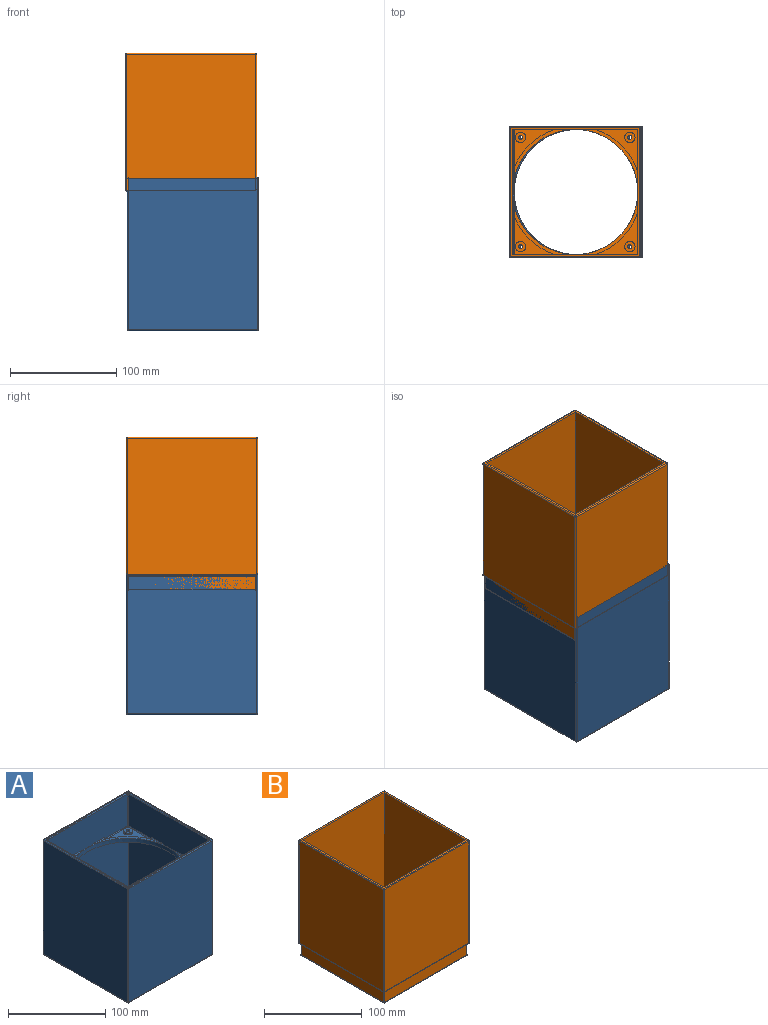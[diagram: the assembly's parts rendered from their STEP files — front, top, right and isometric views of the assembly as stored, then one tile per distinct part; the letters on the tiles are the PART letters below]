
ASSEMBLY  parts=2 mates=1
PART A: 108 faces, bbox 124.4x124.4x145.4 mm
  f0: plane 47.18x47.18mm, normal (0,0,1), area 183.2mm2, adj f14,f21,f98,f100,f105,f107
  f1: plane 47.18x47.18mm, normal (0,0,1), area 183.2mm2, adj f14,f29,f70,f71,f76,f77
  f2: plane 47.18x47.18mm, normal (0,0,1), area 183.2mm2, adj f14,f25,f62,f63,f66,f67
  f3: plane 9.8x9.8mm, normal (0,0,1), area 64.1mm2, adj f13,f31
  f4: plane 9.8x9.8mm, normal (0,0,1), area 64.1mm2, adj f11,f28
  f5: plane 47.18x47.18mm, normal (0,0,1), area 183.2mm2, adj f14,f33,f74,f75,f79,f80
  f6: plane 9.8x9.8mm, normal (0,0,1), area 64.1mm2, adj f12,f22
  f7: plane 9.8x9.8mm, normal (0,0,1), area 64.1mm2, adj f15,f19
  f8: plane 143x122mm, normal (1,0,0), area 17446mm2, adj f43,f44,f53,f54
  f9: plane 143x122mm, normal (0,1,0), area 17446mm2, adj f40,f44,f45,f46
  f10: plane 143x122mm, normal (-1,0,0), area 17446mm2, adj f46,f47,f55,f56
  f11: cylinder r=1.9mm len=5mm, axis (0,0,-1), area 59.7mm2, adj f4,f17
  f12: cylinder r=1.9mm len=5mm, axis (0,0,-1), area 59.7mm2, adj f6,f17
  f13: cylinder r=1.9mm len=5mm, axis (0,0,-1), area 59.7mm2, adj f3,f17
  f14: cylinder r=59mm len=118mm, axis (0,0,-1), area 1853.5mm2, adj f0,f1,f2,f5,f17,f60,f61,f64
  f15: cylinder r=1.9mm len=5mm, axis (0,0,-1), area 59.7mm2, adj f7,f17
  f16: plane 143x122mm, normal (0,-1,0), area 17446mm2, adj f48,f53,f56,f59
  f17: plane 121x121mm, normal (0,0,-1), area 3659.8mm2, adj f11,f12,f13,f14,f15,f35,f36,f37
  f18: plane 34.4x34.4mm, normal (0,0,1), area 385.9mm2, adj f19,f21,f100,f102,f104,f105
  f19: cylinder r=4.9mm len=9.8mm, axis (0,0,-1), area 61.6mm2, adj f7,f18
  f20: plane 116.35x40.35mm, normal (0,-1,0), area 4550mm2, adj f69,f75,f80,f85,f92,f95,f97,f98
  f21: cylinder r=62mm len=32.87mm, axis (0,0,-1), area 95.3mm2, adj f0,f18,f100,f105
  f22: cylinder r=4.9mm len=9.8mm, axis (0,0,-1), area 61.6mm2, adj f6,f24
  f23: plane 116.35x40.35mm, normal (-1,0,0), area 4550mm2, adj f61,f63,f67,f68,f73,f74,f79,f83
  f24: plane 34.4x34.4mm, normal (0,0,1), area 385.9mm2, adj f22,f25,f66,f67,f72,f73
  f25: cylinder r=62mm len=32.87mm, axis (0,0,-1), area 95.3mm2, adj f2,f24,f66,f67
  f26: plane 34.4x34.4mm, normal (0,0,1), area 385.9mm2, adj f28,f29,f76,f77,f81,f82
  f27: plane 116.35x40.35mm, normal (1,0,0), area 4550mm2, adj f64,f70,f76,f81,f89,f96,f101,f104
  f28: cylinder r=4.9mm len=9.8mm, axis (0,0,-1), area 61.6mm2, adj f4,f26
  f29: cylinder r=62mm len=32.87mm, axis (0,0,-1), area 95.3mm2, adj f1,f26,f76,f77
  f30: plane 116.35x40.35mm, normal (0,1,0), area 4550mm2, adj f60,f62,f65,f66,f71,f72,f77,f82
  f31: cylinder r=4.9mm len=9.8mm, axis (0,0,-1), area 61.6mm2, adj f3,f32
  f32: plane 34.4x34.4mm, normal (0,0,1), area 385.9mm2, adj f31,f33,f79,f80,f84,f85
  f33: cylinder r=62mm len=32.87mm, axis (0,0,-1), area 95.3mm2, adj f5,f32,f79,f80
  f34: plane 122x122mm, normal (0,0,1), area 487.4mm2, adj f40,f43,f47,f48,f87,f90,f91,f93
  f35: plane 121x100mm, normal (1,0,0), area 12100mm2, adj f17,f36,f38,f39
  f36: plane 121x100mm, normal (0,1,0), area 12100mm2, adj f17,f35,f37,f39
  f37: plane 121x100mm, normal (-1,0,0), area 12100mm2, adj f17,f36,f38,f39
  f38: plane 121x100mm, normal (0,-1,0), area 12100mm2, adj f17,f35,f37,f39
  f39: plane 122x122mm, normal (0,0,-1), area 243mm2, adj f35,f36,f37,f38,f45,f54,f55,f59
  f40: cylinder r=1mm len=122mm, axis (1,0,0), area 191.6mm2, adj f9,f34,f41,f42
  f41: sphere r=1mm, area 1.6mm2, adj f40,f43,f44
  f42: sphere r=1mm, area 1.6mm2, adj f40,f46,f47
  f43: cylinder r=1mm len=122mm, axis (0,-1,0), area 191.6mm2, adj f8,f34,f41,f49
  f44: cylinder r=1mm len=143mm, axis (0,0,1), area 224.6mm2, adj f8,f9,f41,f50
  f45: cylinder r=1mm len=122mm, axis (1,0,0), area 191.6mm2, adj f9,f39,f50,f51
  f46: cylinder r=1mm len=143mm, axis (0,0,-1), area 224.6mm2, adj f9,f10,f42,f51
  f47: cylinder r=1mm len=122mm, axis (0,1,0), area 191.6mm2, adj f10,f34,f42,f52
  f48: cylinder r=1mm len=122mm, axis (-1,0,0), area 191.6mm2, adj f16,f34,f49,f52
  f49: sphere r=1mm, area 1.6mm2, adj f43,f48,f53
  f50: sphere r=1mm, area 1.6mm2, adj f44,f45,f54
  f51: sphere r=1mm, area 1.6mm2, adj f45,f46,f55
  f52: sphere r=1mm, area 1.6mm2, adj f47,f48,f56
  f53: cylinder r=1mm len=143mm, axis (0,0,-1), area 224.6mm2, adj f8,f16,f49,f57
  f54: cylinder r=1mm len=122mm, axis (0,-1,0), area 191.6mm2, adj f8,f39,f50,f57
  f55: cylinder r=1mm len=122mm, axis (0,1,0), area 191.6mm2, adj f10,f39,f51,f58
  f56: cylinder r=1mm len=143mm, axis (0,0,1), area 224.6mm2, adj f10,f16,f52,f58
  f57: sphere r=1mm, area 1.6mm2, adj f53,f54,f59
  f58: sphere r=1mm, area 1.6mm2, adj f55,f56,f59
  f59: cylinder r=1mm len=122mm, axis (-1,0,0), area 191.6mm2, adj f16,f39,f57,f58
  f60: bspline ~11.83x1.22mm, area 5.4mm2, adj f14,f30,f62
  f61: bspline ~11.83x1.22mm, area 5.4mm2, adj f14,f23,f63
  f62: cylinder r=1mm len=13.78mm, axis (-1,0,0), area 20.9mm2, adj f2,f30,f60,f66
  f63: cylinder r=1mm len=13.78mm, axis (0,-1,0), area 20.9mm2, adj f2,f23,f61,f67
  f64: bspline ~11.83x1.22mm, area 5.4mm2, adj f14,f27,f70
  f65: bspline ~11.83x1.22mm, area 5.4mm2, adj f14,f30,f71
  f66: cylinder r=1mm len=3mm, axis (0,0,-1), area 5.5mm2, adj f2,f24,f25,f30,f62,f72
  f67: cylinder r=1mm len=3mm, axis (0,0,-1), area 5.5mm2, adj f2,f23,f24,f25,f63,f73
  f68: bspline ~11.83x1.22mm, area 5.4mm2, adj f14,f23,f74
  f69: bspline ~11.83x1.22mm, area 5.4mm2, adj f14,f20,f75
  f70: cylinder r=1mm len=13.78mm, axis (0,1,0), area 20.9mm2, adj f1,f27,f64,f76
  f71: cylinder r=1mm len=13.78mm, axis (-1,0,0), area 20.9mm2, adj f1,f30,f65,f77
  f72: cylinder r=1mm len=34.4mm, axis (-1,0,0), area 53.3mm2, adj f24,f30,f66,f78
  f73: cylinder r=1mm len=34.4mm, axis (0,-1,0), area 53.3mm2, adj f23,f24,f67,f78
  f74: cylinder r=1mm len=13.78mm, axis (0,-1,0), area 20.9mm2, adj f5,f23,f68,f79
  f75: cylinder r=1mm len=13.78mm, axis (1,0,0), area 20.9mm2, adj f5,f20,f69,f80
  f76: cylinder r=1mm len=3mm, axis (0,0,-1), area 5.5mm2, adj f1,f26,f27,f29,f70,f81
  f77: cylinder r=1mm len=3mm, axis (0,0,-1), area 5.5mm2, adj f1,f26,f29,f30,f71,f82
  f78: sphere r=1mm, area 1.6mm2, adj f72,f73,f83
  f79: cylinder r=1mm len=3mm, axis (0,0,-1), area 5.5mm2, adj f5,f23,f32,f33,f74,f84
  f80: cylinder r=1mm len=3mm, axis (0,0,-1), area 5.5mm2, adj f5,f20,f32,f33,f75,f85
  f81: cylinder r=1mm len=34.4mm, axis (0,1,0), area 53.3mm2, adj f26,f27,f76,f86
  f82: cylinder r=1mm len=34.4mm, axis (-1,0,0), area 53.3mm2, adj f26,f30,f77,f86
  f83: cylinder r=1mm len=40mm, axis (0,0,1), area 62.8mm2, adj f23,f30,f78,f87
  f84: cylinder r=1mm len=34.4mm, axis (0,-1,0), area 53.3mm2, adj f23,f32,f79,f88
  f85: cylinder r=1mm len=34.4mm, axis (1,0,0), area 53.3mm2, adj f20,f32,f80,f88
  f86: sphere r=1mm, area 1.6mm2, adj f81,f82,f89
  f87: torus R=2mm, axis (0,0,1), area 3.4mm2, adj f34,f83,f90,f91
  f88: sphere r=1mm, area 1.6mm2, adj f84,f85,f92
  f89: cylinder r=1mm len=40mm, axis (0,0,-1), area 62.8mm2, adj f27,f30,f86,f93
  f90: cylinder r=1mm len=116mm, axis (1,0,0), area 182.2mm2, adj f30,f34,f87,f93
  f91: cylinder r=1mm len=116mm, axis (0,1,0), area 182.2mm2, adj f23,f34,f87,f94
  f92: cylinder r=1mm len=40mm, axis (0,0,-1), area 62.8mm2, adj f20,f23,f88,f94
  f93: torus R=2mm, axis (0,0,1), area 3.4mm2, adj f34,f89,f90,f96
  f94: torus R=2mm, axis (0,0,1), area 3.4mm2, adj f34,f91,f92,f97
  f95: bspline ~11.83x1.22mm, area 5.4mm2, adj f14,f20,f98
  f96: cylinder r=1mm len=116mm, axis (0,-1,0), area 182.2mm2, adj f27,f34,f93,f99
  f97: cylinder r=1mm len=116mm, axis (-1,0,0), area 182.2mm2, adj f20,f34,f94,f99
  f98: cylinder r=1mm len=13.78mm, axis (1,0,0), area 20.9mm2, adj f0,f20,f95,f100
  f99: torus R=2mm, axis (0,0,1), area 3.4mm2, adj f34,f96,f97,f101
  f100: cylinder r=1mm len=3mm, axis (0,0,-1), area 5.5mm2, adj f0,f18,f20,f21,f98,f102
  f101: cylinder r=1mm len=40mm, axis (0,0,1), area 62.8mm2, adj f20,f27,f99,f103
  f102: cylinder r=1mm len=34.4mm, axis (1,0,0), area 53.3mm2, adj f18,f20,f100,f103
  f103: sphere r=1mm, area 1.6mm2, adj f101,f102,f104
  f104: cylinder r=1mm len=34.4mm, axis (0,1,0), area 53.3mm2, adj f18,f27,f103,f105
  f105: cylinder r=1mm len=3mm, axis (0,0,-1), area 5.5mm2, adj f0,f18,f21,f27,f104,f107
  f106: bspline ~11.83x1.22mm, area 5.4mm2, adj f14,f27,f107
  f107: cylinder r=1mm len=13.78mm, axis (0,1,0), area 20.9mm2, adj f0,f27,f105,f106
PART B: 103 faces, bbox 124.9x124.9x145 mm
  f0: plane 0.18x0.18mm, normal (0,0,-1), area 0mm2, adj f58,f85,f86
  f1: plane 0.18x0.18mm, normal (0,0,-1), area 0mm2, adj f49,f73,f74
  f2: plane 0.18x0.18mm, normal (0,0,-1), area 0mm2, adj f59,f75,f76
  f3: plane 119x119mm, normal (0,0,-1), area 3179.8mm2, adj f15,f16,f17,f18,f19,f42,f43,f44
  f4: plane 59x59mm, normal (0,0,1), area 208.5mm2, adj f18,f24,f25,f31
  f5: plane 59x59mm, normal (0,0,1), area 208.5mm2, adj f18,f31,f33,f34
  f6: plane 59x59mm, normal (0,0,1), area 208.5mm2, adj f18,f27,f29,f34
  f7: plane 9.8x9.8mm, normal (0,0,1), area 64.1mm2, adj f17,f35
  f8: plane 9.8x9.8mm, normal (0,0,1), area 64.1mm2, adj f15,f32
  f9: plane 59x59mm, normal (0,0,1), area 208.5mm2, adj f18,f24,f27,f37
  f10: plane 9.8x9.8mm, normal (0,0,1), area 64.1mm2, adj f16,f26
  f11: plane 9.8x9.8mm, normal (0,0,1), area 64.1mm2, adj f19,f23
  f12: plane 128.06x122mm, normal (1,0,0), area 15623.6mm2, adj f67,f69,f70,f74,f75,f87,f88,f89
  f13: plane 128.06x122mm, normal (0,1,0), area 15623.6mm2, adj f68,f72,f73,f80,f86,f87,f96,f97
  f14: plane 128.06x122mm, normal (-1,0,0), area 15623.6mm2, adj f78,f79,f84,f85,f91,f96,f99,f102
  f15: cylinder r=1.9mm len=5mm, axis (0,0,-1), area 59.7mm2, adj f3,f8
  f16: cylinder r=1.9mm len=5mm, axis (0,0,-1), area 59.7mm2, adj f3,f10
  f17: cylinder r=1.9mm len=5mm, axis (0,0,-1), area 59.7mm2, adj f3,f7
  f18: cylinder r=59mm len=118mm, axis (0,0,-1), area 1853.5mm2, adj f3,f4,f5,f6,f9
  f19: cylinder r=1.9mm len=5mm, axis (0,0,-1), area 59.7mm2, adj f3,f11
  f20: plane 128.06x122mm, normal (0,-1,0), area 15623.6mm2, adj f71,f76,f77,f83,f89,f90,f98,f99
  f21: plane 0.18x0.18mm, normal (0,0,-1), area 0mm2, adj f65,f90,f91
  f22: plane 39.95x39.95mm, normal (0,0,1), area 463.1mm2, adj f23,f24,f25,f31
  f23: cylinder r=4.9mm len=9.8mm, axis (0,0,-1), area 61.6mm2, adj f11,f22
  f24: plane 127x118mm, normal (0,-1,0), area 14909.8mm2, adj f4,f9,f22,f25,f27,f31,f36,f37
  f25: cylinder r=62mm len=39.95mm, axis (0,0,-1), area 117.3mm2, adj f4,f22,f24,f31
  f26: cylinder r=4.9mm len=9.8mm, axis (0,0,-1), area 61.6mm2, adj f10,f28
  f27: plane 127x118mm, normal (-1,0,0), area 14909.8mm2, adj f6,f9,f24,f28,f29,f34,f36,f37
  f28: plane 39.95x39.95mm, normal (0,0,1), area 463.1mm2, adj f26,f27,f29,f34
  f29: cylinder r=62mm len=39.95mm, axis (0,0,-1), area 117.3mm2, adj f6,f27,f28,f34
  f30: plane 39.95x39.95mm, normal (0,0,1), area 463.1mm2, adj f31,f32,f33,f34
  f31: plane 127x118mm, normal (1,0,0), area 14909.8mm2, adj f4,f5,f22,f24,f25,f30,f33,f34
  f32: cylinder r=4.9mm len=9.8mm, axis (0,0,-1), area 61.6mm2, adj f8,f30
  f33: cylinder r=62mm len=39.95mm, axis (0,0,-1), area 117.3mm2, adj f5,f30,f31,f34
  f34: plane 127x118mm, normal (0,1,0), area 14909.8mm2, adj f5,f6,f27,f28,f29,f30,f31,f33
  f35: cylinder r=4.9mm len=9.8mm, axis (0,0,-1), area 61.6mm2, adj f7,f36
  f36: plane 39.95x39.95mm, normal (0,0,1), area 463.1mm2, adj f24,f27,f35,f37
  f37: cylinder r=62mm len=39.95mm, axis (0,0,-1), area 117.3mm2, adj f9,f24,f27,f36
  f38: plane 122x122mm, normal (0,0,1), area 960mm2, adj f24,f27,f31,f34,f88,f97,f98,f102
  f39: plane 119x13mm, normal (0,-1,0), area 1547mm2, adj f55,f60,f63,f66
  f40: plane 119x13mm, normal (-1,0,0), area 1547mm2, adj f52,f61,f62,f66
  f41: plane 119x13mm, normal (0,1,0), area 1547mm2, adj f47,f51,f52,f53
  f42: plane 119x15mm, normal (0,-1,0), area 1785mm2, adj f3,f43,f45,f51
  f43: plane 119x15mm, normal (1,0,0), area 1785mm2, adj f3,f42,f44,f61
  f44: plane 119x15mm, normal (0,1,0), area 1785mm2, adj f3,f43,f45,f60
  f45: plane 119x15mm, normal (-1,0,0), area 1785mm2, adj f3,f42,f44,f50
  f46: plane 119x13mm, normal (1,0,0), area 1547mm2, adj f47,f50,f54,f55
  f47: cylinder r=1mm len=13mm, axis (0,0,-1), area 20.4mm2, adj f41,f46,f48,f49
  f48: sphere r=1mm, area 1.6mm2, adj f47,f50,f51
  f49: torus R=2mm, axis (0,0,1), area 3mm2, adj f1,f47,f53,f54,f68,f69
  f50: cylinder r=1mm len=119mm, axis (0,1,0), area 186.9mm2, adj f45,f46,f48,f56
  f51: cylinder r=1mm len=119mm, axis (-1,0,0), area 186.9mm2, adj f41,f42,f48,f57
  f52: cylinder r=1mm len=13mm, axis (0,0,1), area 20.4mm2, adj f40,f41,f57,f58
  f53: cylinder r=1mm len=119mm, axis (-1,0,0), area 156.9mm2, adj f41,f49,f58,f72
  f54: cylinder r=1mm len=119mm, axis (0,1,0), area 156.9mm2, adj f46,f49,f59,f67
  f55: cylinder r=1mm len=13mm, axis (0,0,1), area 20.4mm2, adj f39,f46,f56,f59
  f56: sphere r=1mm, area 1.6mm2, adj f50,f55,f60
  f57: sphere r=1mm, area 1.6mm2, adj f51,f52,f61
  f58: torus R=2mm, axis (0,0,1), area 3mm2, adj f0,f52,f53,f62,f79,f80
  f59: torus R=2mm, axis (0,0,1), area 3mm2, adj f2,f54,f55,f63,f70,f71
  f60: cylinder r=1mm len=119mm, axis (1,0,0), area 186.9mm2, adj f39,f44,f56,f64
  f61: cylinder r=1mm len=119mm, axis (0,-1,0), area 186.9mm2, adj f40,f43,f57,f64
  f62: cylinder r=1mm len=119mm, axis (0,-1,0), area 156.9mm2, adj f40,f58,f65,f78
  f63: cylinder r=1mm len=119mm, axis (1,0,0), area 156.9mm2, adj f39,f59,f65,f77
  f64: sphere r=1mm, area 1.6mm2, adj f60,f61,f66
  f65: torus R=2mm, axis (0,0,1), area 3mm2, adj f21,f62,f63,f66,f83,f84
  f66: cylinder r=1mm len=13mm, axis (0,0,-1), area 20.4mm2, adj f39,f40,f64,f65
  f67: cylinder r=1mm len=119mm, axis (0,1,0), area 156.9mm2, adj f12,f54,f69,f70
  f68: bspline ~2.17x1.12mm, area 1.9mm2, adj f13,f49,f72,f73
  f69: bspline ~2.17x1.12mm, area 1.9mm2, adj f12,f49,f67,f74
  f70: bspline ~2.57x1.19mm, area 1.9mm2, adj f12,f59,f67,f75
  f71: bspline ~2.17x1.12mm, area 1.9mm2, adj f20,f59,f76,f77
  f72: cylinder r=1mm len=119mm, axis (-1,0,0), area 156.9mm2, adj f13,f53,f68,f80
  f73: cylinder r=1mm len=1mm, axis (-1,0,0), area 0.3mm2, adj f1,f13,f68,f81
  f74: cylinder r=1mm len=1mm, axis (0,1,0), area 0.3mm2, adj f1,f12,f69,f81
  f75: cylinder r=1mm len=1mm, axis (0,1,0), area 0.3mm2, adj f2,f12,f70,f82
  f76: cylinder r=1mm len=1mm, axis (1,0,0), area 0.3mm2, adj f2,f20,f71,f82
  f77: cylinder r=1mm len=119mm, axis (1,0,0), area 156.9mm2, adj f20,f63,f71,f83
  f78: cylinder r=1mm len=119mm, axis (0,-1,0), area 156.9mm2, adj f14,f62,f79,f84
  f79: bspline ~2.17x1.12mm, area 1.9mm2, adj f14,f58,f78,f85
  f80: bspline ~2.57x1.19mm, area 1.9mm2, adj f13,f58,f72,f86
  f81: sphere r=1mm, area 1.6mm2, adj f73,f74,f87
  f82: sphere r=1mm, area 1.6mm2, adj f75,f76,f89
  f83: bspline ~2.57x1.19mm, area 1.9mm2, adj f20,f65,f77,f90
  f84: bspline ~2.57x1.19mm, area 1.9mm2, adj f14,f65,f78,f91
  f85: cylinder r=1mm len=1mm, axis (0,-1,0), area 0.3mm2, adj f0,f14,f79,f92
  f86: cylinder r=1mm len=1mm, axis (-1,0,0), area 0.3mm2, adj f0,f13,f80,f92
  f87: cylinder r=1mm len=128mm, axis (0,0,1), area 201.1mm2, adj f12,f13,f81,f93
  f88: cylinder r=1mm len=122mm, axis (0,-1,0), area 191.6mm2, adj f12,f38,f93,f94
  f89: cylinder r=1mm len=128mm, axis (0,0,-1), area 201.1mm2, adj f12,f20,f82,f94
  f90: cylinder r=1mm len=1mm, axis (1,0,0), area 0.3mm2, adj f20,f21,f83,f95
  f91: cylinder r=1mm len=1mm, axis (0,-1,0), area 0.3mm2, adj f14,f21,f84,f95
  f92: sphere r=1mm, area 1.6mm2, adj f85,f86,f96
  f93: sphere r=1mm, area 1.6mm2, adj f87,f88,f97
  f94: sphere r=1mm, area 1.6mm2, adj f88,f89,f98
  f95: sphere r=1mm, area 1.6mm2, adj f90,f91,f99
  f96: cylinder r=1mm len=128mm, axis (0,0,-1), area 201.1mm2, adj f13,f14,f92,f100
  f97: cylinder r=1mm len=122mm, axis (1,0,0), area 191.6mm2, adj f13,f38,f93,f100
  f98: cylinder r=1mm len=122mm, axis (-1,0,0), area 191.6mm2, adj f20,f38,f94,f101
  f99: cylinder r=1mm len=128mm, axis (0,0,1), area 201.1mm2, adj f14,f20,f95,f101
  f100: sphere r=1mm, area 1.6mm2, adj f96,f97,f102
  f101: sphere r=1mm, area 1.6mm2, adj f98,f99,f102
  f102: cylinder r=1mm len=122mm, axis (0,1,0), area 191.6mm2, adj f14,f38,f100,f101
PLACE A t=(-4.44,13.84,64.61)mm
PLACE B t=(-5.94,13.84,96.42)mm
MATE planar B.f46 <-> A.f23  axis (1,0,0) through (54.56,13.84,88.92)mm
